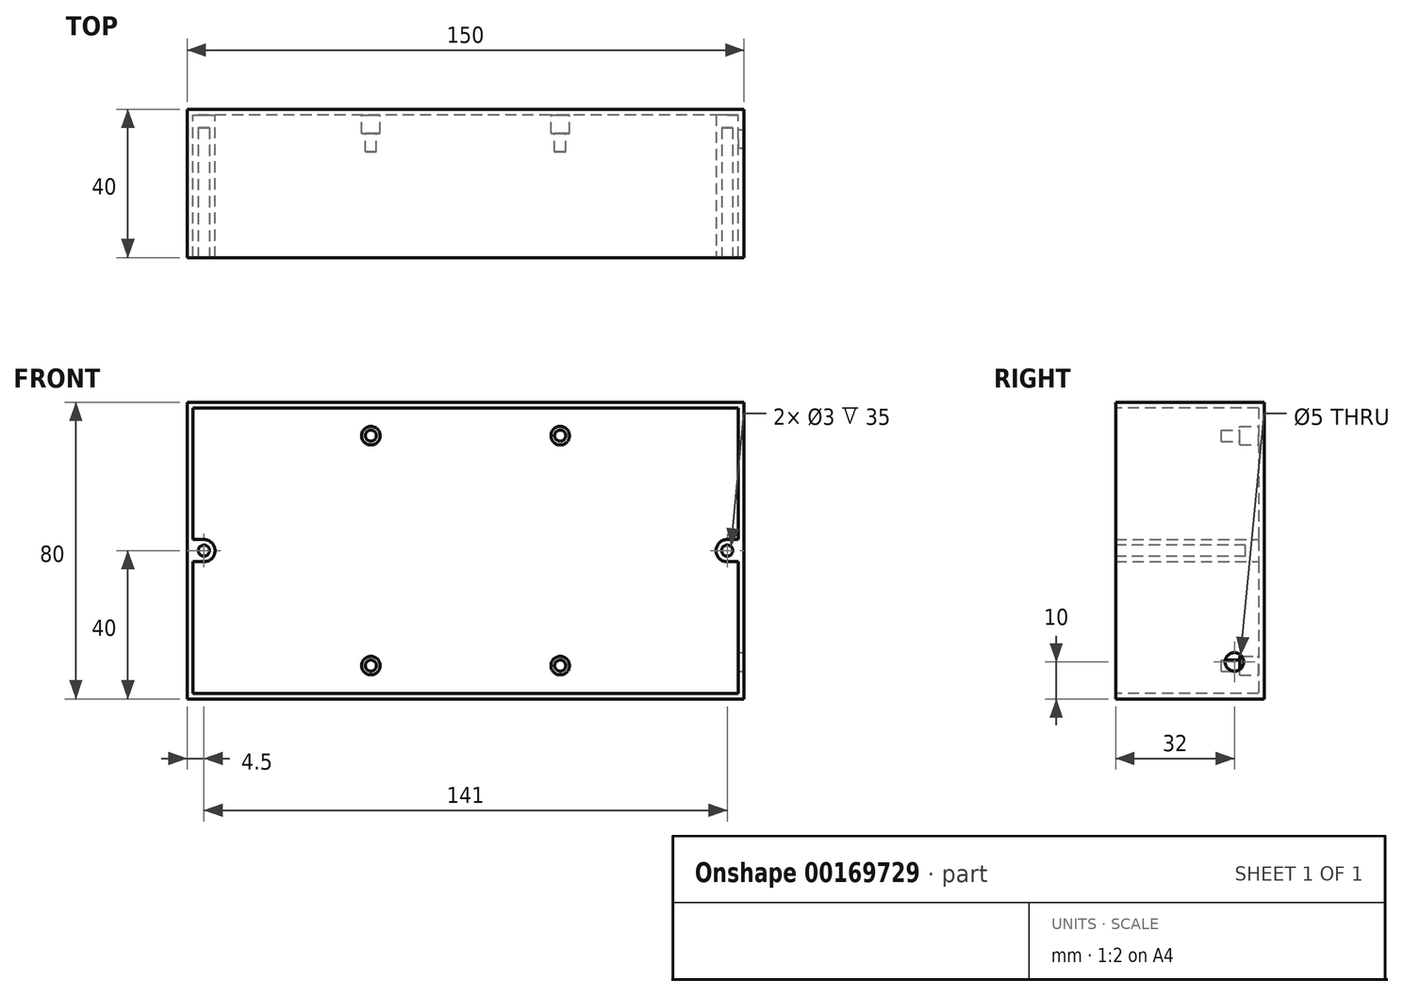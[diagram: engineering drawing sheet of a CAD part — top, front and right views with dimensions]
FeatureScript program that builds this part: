
annotation { "Feature Type Name" : "Feature", "Feature Type Description" : "" }
export const myFeature = defineFeature(function(context is Context, id is Id, definition is map)
    precondition{}
    {
        {
            var Q0;
            Q0=qCreatedBy(makeId("Front.planeOp"),FACE);
            var sketch = newSketch(context, id + "F0", { "sketchPlane" : qUnion([Q0])});
            skLineSegment(sketch, "E0.bottom", {"start": v(-75, 40) * mm, "end": v(75, 40) * mm});
            skLineSegment(sketch, "E0.top", {"start": v(-75, -40) * mm, "end": v(75, -40) * mm});
            skLineSegment(sketch, "E0.left", {"start": v(-75, 40) * mm, "end": v(-75, -40) * mm});
            skLineSegment(sketch, "E0.right", {"start": v(75, 40) * mm, "end": v(75, -40) * mm});
            skSolve(sketch);
        }
        {
            var Q0;
            Q0=makeQuery(id+"F0.imprint","IMPRINT",FACE,{"disambiguationData":[TD([[makeQuery(id+"F0.imprint","IMPRINT",EDGE,{"derivedFrom":sQuery(id+"F0.wireOp",EDGE,"E0.bottom")}),-1.0]])]});
            extrude(context, id + "F1", {"entities" : qUnion([Q0]), "depth" : 40 * mm});
        }
        {
            var Q0;
            Q0=makeQuery(id+"F1.opExtrude","CAP_FACE",FACE,{"disambiguationData":[OSD([sQuery(id+"F0.wireOp",EDGE,"E0.bottom"),sQuery(id+"F0.wireOp",EDGE,"E0.top"),sQuery(id+"F0.wireOp",EDGE,"E0.left"),sQuery(id+"F0.wireOp",EDGE,"E0.right")])],"isStart":false});
            var sketch = newSketch(context, id + "F2", { "sketchPlane" : qUnion([Q0])});
            skLineSegment(sketch, "E1.bottom", {"start": v(73.5, 38.5) * mm, "end": v(-73.5, 38.5) * mm});
            skLineSegment(sketch, "E1.top", {"start": v(73.5, -38.5) * mm, "end": v(-73.5, -38.5) * mm});
            skLineSegment(sketch, "E1.left", {"start": v(73.5, 38.5) * mm, "end": v(73.5, -38.5) * mm});
            skLineSegment(sketch, "E1.right", {"start": v(-73.5, 38.5) * mm, "end": v(-73.5, -38.5) * mm});
            skSolve(sketch);
        }
        {
            var Q0;
            Q0=makeQuery(id+"F2.imprint","IMPRINT",FACE,{"disambiguationData":[TD([[makeQuery(id+"F2.imprint","IMPRINT",EDGE,{"derivedFrom":sQuery(id+"F2.wireOp",EDGE,"E1.bottom")}),1.0]])]});
            extrude(context, id + "F3", {"entities" : qUnion([Q0]), "operationType" : NewBodyOperationType.REMOVE, "oppositeDirection" : true, "depth" : 38.5 * mm});
        }
        {
            var Q0;
            Q0=makeQuery(id+"F3.boolean.opBoolean","COPY",FACE,{"derivedFrom":makeQuery(id+"F3.opExtrude","CAP_FACE",FACE,{"disambiguationData":[OSD([sQuery(id+"F2.wireOp",EDGE,"E1.bottom"),sQuery(id+"F2.wireOp",EDGE,"E1.top"),sQuery(id+"F2.wireOp",EDGE,"E1.left"),sQuery(id+"F2.wireOp",EDGE,"E1.right")])],"isStart":false})});
            var sketch = newSketch(context, id + "F4", { "sketchPlane" : qUnion([Q0])});
            skCircle(sketch, "E2", {"center": v(-25.5, 31) * mm, "radius": 2.5 * mm});
            skCircle(sketch, "E3", {"center": v(-25.5, -31) * mm, "radius": 2.5 * mm});
            skCircle(sketch, "E4", {"center": v(25.5, 31) * mm, "radius": 2.5 * mm});
            skCircle(sketch, "E5", {"center": v(25.5, -31) * mm, "radius": 2.5 * mm});
            skSolve(sketch);
        }
        {
            var Q0;
            Q0 = qSketchRegion(id + "F4", true);
            extrude(context, id + "F5", {"entities" : qUnion([Q0]), "operationType" : NewBodyOperationType.ADD, "depth" : 5 * mm});
        }
        {
            var Q0;
            Q0=makeQuery(id+"F5.opExtrude","CAP_FACE",FACE,{"disambiguationData":[OSD([sQuery(id+"F4.wireOp",EDGE,"E2")])],"isStart":false});
            var sketch = newSketch(context, id + "F6", { "sketchPlane" : qUnion([Q0])});
            skCircle(sketch, "E6", {"center": v(-25.5, 31) * mm, "radius": 1.5 * mm});
            skSolve(sketch);
        }
        {
            var Q0;
            Q0=makeQuery(id+"F5.opExtrude","CAP_FACE",FACE,{"disambiguationData":[OSD([sQuery(id+"F4.wireOp",EDGE,"E4")])],"isStart":false});
            var sketch = newSketch(context, id + "F7", { "sketchPlane" : qUnion([Q0])});
            skCircle(sketch, "E7", {"center": v(25.5, 31) * mm, "radius": 1.5 * mm});
            skSolve(sketch);
        }
        {
            var Q0;
            Q0=makeQuery(id+"F5.opExtrude","CAP_FACE",FACE,{"disambiguationData":[OSD([sQuery(id+"F4.wireOp",EDGE,"E3")])],"isStart":false});
            var sketch = newSketch(context, id + "F8", { "sketchPlane" : qUnion([Q0])});
            skCircle(sketch, "E8", {"center": v(-25.5, -31) * mm, "radius": 1.5 * mm});
            skSolve(sketch);
        }
        {
            var Q0;
            Q0=makeQuery(id+"F5.opExtrude","CAP_FACE",FACE,{"disambiguationData":[OSD([sQuery(id+"F4.wireOp",EDGE,"E5")])],"isStart":false});
            var sketch = newSketch(context, id + "F9", { "sketchPlane" : qUnion([Q0])});
            skCircle(sketch, "E9", {"center": v(25.5, -31) * mm, "radius": 1.5 * mm});
            skSolve(sketch);
        }
        {
            var Q0;
            Q0 = qSketchRegion(id + "F6", true);
            var Q1;
            Q1 = qSketchRegion(id + "F7", true);
            var Q2;
            Q2 = qSketchRegion(id + "F8", true);
            var Q3;
            Q3 = qSketchRegion(id + "F9", true);
            extrude(context, id + "F10", {"entities" : qUnion([Q0, Q1, Q2, Q3]), "operationType" : NewBodyOperationType.ADD, "depth" : 5 * mm});
        }
        {
            var Q0;
            Q0=makeQuery(id+"F1.opExtrude","SWEPT_FACE",FACE,{"disambiguationData":[OSD([sQuery(id+"F0.wireOp",EDGE,"E0.right")])]});
            var sketch = newSketch(context, id + "F11", { "sketchPlane" : qUnion([Q0])});
            skCircle(sketch, "E10", {"center": v(-8, -30) * mm, "radius": 2.5 * mm});
            skSolve(sketch);
        }
        {
            var Q0;
            Q0 = qSketchRegion(id + "F11", true);
            extrude(context, id + "F12", {"entities" : qUnion([Q0]), "operationType" : NewBodyOperationType.REMOVE, "oppositeDirection" : true, "depth" : 3 * mm});
        }
        {
            var Q0;
            Q0=makeQuery(id+"F3.boolean.opBoolean","COPY",FACE,{"derivedFrom":makeQuery(id+"F3.opExtrude","CAP_FACE",FACE,{"disambiguationData":[OSD([sQuery(id+"F2.wireOp",EDGE,"E1.bottom"),sQuery(id+"F2.wireOp",EDGE,"E1.top"),sQuery(id+"F2.wireOp",EDGE,"E1.left"),sQuery(id+"F2.wireOp",EDGE,"E1.right")])],"isStart":false})});
            var sketch = newSketch(context, id + "F13", { "sketchPlane" : qUnion([Q0])});
            skLineSegment(sketch, "E11.bottom", {"start": v(-73.5, 3) * mm, "end": v(-67.5, 3) * mm});
            skLineSegment(sketch, "E11.top", {"start": v(-73.5, -3) * mm, "end": v(-67.5, -3) * mm});
            skLineSegment(sketch, "E11.left", {"start": v(-73.5, 3) * mm, "end": v(-73.5, -3) * mm});
            skLineSegment(sketch, "E11.right", {"start": v(-67.5, 3) * mm, "end": v(-67.5, -3) * mm});
            skLineSegment(sketch, "E12.bottom", {"start": v(67.5, -3) * mm, "end": v(73.5, -3) * mm});
            skLineSegment(sketch, "E12.top", {"start": v(67.5, 3) * mm, "end": v(73.5, 3) * mm});
            skLineSegment(sketch, "E12.left", {"start": v(67.5, -3) * mm, "end": v(67.5, 3) * mm});
            skLineSegment(sketch, "E12.right", {"start": v(73.5, -3) * mm, "end": v(73.5, 3) * mm});
            skSolve(sketch);
        }
        {
            var Q0;
            Q0 = qSketchRegion(id + "F13", true);
            extrude(context, id + "F14", {"entities" : qUnion([Q0]), "operationType" : NewBodyOperationType.ADD, "depth" : 38.5 * mm});
        }
        {
            var Q0;
            Q0=makeQuery(id+"F14.boolean.opBoolean","MERGE",FACE,{"derivedFrom":[makeQuery(id+"F1.opExtrude","CAP_FACE",FACE,{"disambiguationData":[OSD([sQuery(id+"F0.wireOp",EDGE,"E0.bottom"),sQuery(id+"F0.wireOp",EDGE,"E0.top"),sQuery(id+"F0.wireOp",EDGE,"E0.left"),sQuery(id+"F0.wireOp",EDGE,"E0.right")])],"isStart":true}),makeQuery(id+"F14.opExtrude","CAP_FACE",FACE,{"disambiguationData":[OSD([sQuery(id+"F13.wireOp",EDGE,"E11.bottom"),sQuery(id+"F13.wireOp",EDGE,"E11.top"),sQuery(id+"F13.wireOp",EDGE,"E11.left"),sQuery(id+"F13.wireOp",EDGE,"E11.right")])],"isStart":false}),makeQuery(id+"F14.opExtrude","CAP_FACE",FACE,{"disambiguationData":[OSD([sQuery(id+"F13.wireOp",EDGE,"E12.bottom"),sQuery(id+"F13.wireOp",EDGE,"E12.top"),sQuery(id+"F13.wireOp",EDGE,"E12.left"),sQuery(id+"F13.wireOp",EDGE,"E12.right")])],"isStart":false})]});
            var sketch = newSketch(context, id + "F15", { "sketchPlane" : qUnion([Q0])});
            skCircle(sketch, "E13", {"center": v(-70.5, 0) * mm, "radius": 1.5 * mm});
            skCircle(sketch, "E14", {"center": v(70.5, 0) * mm, "radius": 1.5 * mm});
            skSolve(sketch);
        }
        {
            var Q0;
            Q0 = qSketchRegion(id + "F15", true);
            extrude(context, id + "F16", {"entities" : qUnion([Q0]), "operationType" : NewBodyOperationType.REMOVE, "oppositeDirection" : true, "depth" : 35 * mm});
        }
        {
            var Q0;
            Q0=makeQuery(id+"F14.opExtrude","SWEPT_EDGE",EDGE,{"disambiguationData":[OSD([sQuery(id+"F13.wireOp",EDGE,"E11.bottom"),sQuery(id+"F13.wireOp",EDGE,"E11.right")])]});
            var Q1;
            Q1=makeQuery(id+"F14.opExtrude","SWEPT_EDGE",EDGE,{"disambiguationData":[OSD([sQuery(id+"F13.wireOp",EDGE,"E11.top"),sQuery(id+"F13.wireOp",EDGE,"E11.right")])]});
            var Q2;
            Q2=makeQuery(id+"F14.opExtrude","SWEPT_EDGE",EDGE,{"disambiguationData":[OSD([sQuery(id+"F13.wireOp",EDGE,"E12.bottom"),sQuery(id+"F13.wireOp",EDGE,"E12.left")])]});
            var Q3;
            Q3=makeQuery(id+"F14.opExtrude","SWEPT_EDGE",EDGE,{"disambiguationData":[OSD([sQuery(id+"F13.wireOp",EDGE,"E12.top"),sQuery(id+"F13.wireOp",EDGE,"E12.left")])]});
            fillet(context, id + "F17", {"entities" : qUnion([Q0, Q1, Q2, Q3]), "radius" : 3 * mm, "tangentPropagation" : true, "allowEdgeOverflow" : false});
        }
    });
